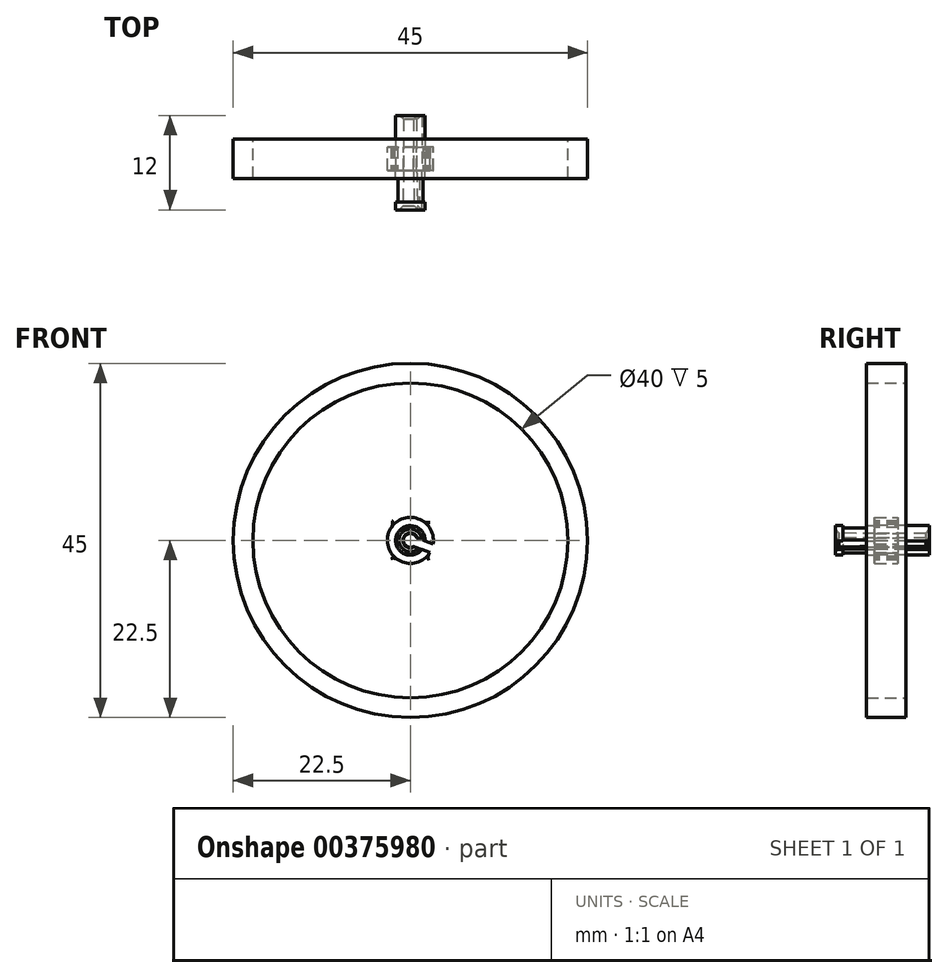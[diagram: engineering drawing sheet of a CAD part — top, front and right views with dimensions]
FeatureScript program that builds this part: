
annotation { "Feature Type Name" : "Feature", "Feature Type Description" : "" }
export const myFeature = defineFeature(function(context is Context, id is Id, definition is map)
    precondition{}
    {
        {
            var Q0;
            Q0=qCreatedBy(makeId("Front.planeOp"),FACE);
            var sketch = newSketch(context, id + "F0", { "sketchPlane" : qUnion([Q0])});
            skCircle(sketch, "E0", {"center": v(0, 0) * mm, "radius": 22.5 * mm});
            skCircle(sketch, "E1", {"center": v(0, 0) * mm, "radius": 0.88 * mm});
            skCircle(sketch, "E2", {"center": v(0, 0) * mm, "radius": 2.92 * mm});
            skCircle(sketch, "E3", {"center": v(0, 0) * mm, "radius": 20 * mm});
            skSolve(sketch);
        }
        {
            var Q0;
            Q0=qSketchRegion(id+"F0",true);
            var Q1;
            Q1=makeQuery(id+"F0.imprint","IMPRINT",FACE,{"disambiguationData":[TD([[makeQuery(id+"F0.imprint","IMPRINT",EDGE,{"derivedFrom":sQuery(id+"F0.wireOp",EDGE,"E1")}),-1.0]])]});
            extrude(context, id + "F1", {"entities" : qUnion([Q0, Q1]), "depth" : 3 * mm});
        }
        {
            var Q0;
            Q0=makeQuery(id+"F1.opExtrude","CAP_FACE",FACE,{"disambiguationData":[OSD([sQuery(id+"F0.wireOp",EDGE,"E0"),sQuery(id+"F0.wireOp",EDGE,"E3")])],"isStart":false});
            var sketch = newSketch(context, id + "F2", { "sketchPlane" : qUnion([Q0])});
            skLineSegment(sketch, "E4", {"start": v(1, 19.97) * mm, "end": v(1.93, 2.2) * mm});
            skLineSegment(sketch, "E5", {"start": v(-1, 19.97) * mm, "end": v(-1.93, 2.2) * mm});
            skLineSegment(sketch, "E6.1.0", {"start": v(-16.8, -10.85) * mm, "end": v(-0.94, -2.77) * mm});
            skLineSegment(sketch, "E6.1.1", {"start": v(-17.8, -9.12) * mm, "end": v(-2.87, 0.57) * mm});
            skLineSegment(sketch, "E6.2.0", {"start": v(17.8, -9.12) * mm, "end": v(2.87, 0.57) * mm});
            skLineSegment(sketch, "E6.2.1", {"start": v(16.8, -10.85) * mm, "end": v(0.94, -2.77) * mm});
            skPoint(sketch, "E6.center", {"position": v(0, 0) * mm});
            skArc(sketch, "E7", {"start": v(-17.8, -9.12) * mm, "mid": v(-17.32, -10) * mm, "end": v(-16.8, -10.85) * mm});
            skCircle(sketch, "E8", {"center": v(0, 0) * mm, "radius": 2.92 * mm});
            skArc(sketch, "E9.trimOffspring", {"start": v(1, 19.97) * mm, "mid": v(0, 20) * mm, "end": v(-1, 19.97) * mm});
            skArc(sketch, "E10.trimOffspring", {"start": v(16.8, -10.85) * mm, "mid": v(17.32, -10) * mm, "end": v(17.8, -9.12) * mm});
            skCircle(sketch, "E11", {"center": v(0, 0) * mm, "radius": 0.88 * mm});
            skSolve(sketch);
        }
        {
            var Q0;
            {var subQ2=sQuery(id+"F2.wireOp",EDGE,"E7");Q0=makeQuery(id+"F2.imprint","IMPRINT",FACE,{"disambiguationData":[TD([[makeQuery(id+"F2.imprint","IMPRINT",EDGE,{"derivedFrom":subQ2}),-1.0]])]});}
            var sketch = newSketch(context, id + "F3", { "sketchPlane" : qUnion([Q0])});
            skFitSpline(sketch, "E12", {"points": [v(-2.13, 2) * mm, v(-2.65, 4.3) * mm, v(-2.74, 9.9) * mm, v(0, 21.11) * mm, v(10.38, 33.43) * mm], "startDerivative": vector(-6.91, 17.48) * mm, "endDerivative": vector(42.25, 24.9) * mm});
            skFitSpline(sketch, "E13.0", {"points": [v(-0.27, 2.74) * mm, v(-0.33, 2.88) * mm, v(-0.41, 3.13) * mm, v(-0.5, 3.47) * mm, v(-0.57, 3.84) * mm, v(-0.64, 4.3) * mm, v(-0.7, 4.89) * mm, v(-0.75, 5.54) * mm, v(-0.79, 6.26) * mm, v(-0.82, 7.3) * mm, v(-0.81, 8.76) * mm, v(-0.69, 10.68) * mm, v(-0.4, 12.76) * mm, v(0.18, 15.7) * mm, v(1.13, 18.79) * mm, v(2.53, 21.89) * mm, v(4.24, 24.93) * mm, v(6.96, 28.48) * mm, v(9.8, 30.76) * mm, v(11.4, 31.7) * mm]});
            skPoint(sketch, "E14.visualSharp", {"position": v(10.36, 33.42) * mm});
            skArc(sketch, "E14.filletArc", {"start": v(7.87, 31.7) * mm, "mid": v(8.44, 32.94) * mm, "end": v(7.78, 34.12) * mm});
            skPoint(sketch, "E15.visualSharp", {"position": v(11.37, 31.7) * mm});
            skArc(sketch, "E15.filletArc", {"start": v(15.2, 31.53) * mm, "mid": v(13.12, 32.1) * mm, "end": v(11.05, 31.5) * mm});
            skArc(sketch, "E16.filletArc", {"start": v(-2.43, 1.63) * mm, "mid": v(-2.27, 2.05) * mm, "end": v(-2.3, 2.5) * mm});
            skPoint(sketch, "E17.visualSharp", {"position": v(-0.33, 2.9) * mm});
            skArc(sketch, "E17.filletArc", {"start": v(-0.46, 3.3) * mm, "mid": v(-0.28, 3.03) * mm, "end": v(0.02, 2.92) * mm});
            skArc(sketch, "E18", {"start": v(0.02, 2.92) * mm, "mid": v(-1.37, 2.59) * mm, "end": v(-2.43, 1.63) * mm});
            skArc(sketch, "E19", {"start": v(15.2, 31.53) * mm, "mid": v(11.57, 33.03) * mm, "end": v(7.78, 34.12) * mm});
            skSolve(sketch);
        }
        {
            var Q0;
            Q0=qSketchRegion(id+"F3",true);
            extrude(context, id + "F4", {"entities" : qUnion([Q0]), "oppositeDirection" : true, "depth" : 3 * mm});
        }
        {
            var Q0;
            Q0=makeQuery(id+"F4.opExtrude","SWEPT_BODY",BODY,{"disambiguationData":[OSD([sQuery(id+"F3.wireOp",EDGE,"E12"),sQuery(id+"F3.wireOp",EDGE,"E13.0"),sQuery(id+"F3.wireOp",EDGE,"E14.filletArc"),sQuery(id+"F3.wireOp",EDGE,"E15.filletArc"),sQuery(id+"F3.wireOp",EDGE,"E16.filletArc"),sQuery(id+"F3.wireOp",EDGE,"E17.filletArc"),sQuery(id+"F3.wireOp",EDGE,"E18"),sQuery(id+"F3.wireOp",EDGE,"E19")])]});
            var Q1;
            Q1=makeQuery(id+"F1.opExtrude","CAP_EDGE",EDGE,{"disambiguationData":[OSD([sQuery(id+"F0.wireOp",EDGE,"E2")])],"isStart":false});
            circularPattern(context, id + "F5", {"entities" : qUnion([Q0]), "axis" : qUnion([Q1]), "angle" : 360 * degree, "instanceCount" : 4, "equalSpace" : true});
        }
        {
            var Q0;
            Q0=makeQuery(id+"F1.opExtrude","CAP_FACE",FACE,{"disambiguationData":[OSD([sQuery(id+"F0.wireOp",EDGE,"E1"),sQuery(id+"F0.wireOp",EDGE,"E2")])],"isStart":false});
            var sketch = newSketch(context, id + "F6", { "sketchPlane" : qUnion([Q0])});
            skSolve(sketch);
        }
        {
            var Q0;
            Q0=makeQuery(id+"F6.imprint","IMPRINT",FACE,{"disambiguationData":[TD([[makeQuery(id+"F6.imprint","IMPRINT",EDGE,{"derivedFrom":makeQuery(id+"F1.opExtrude","CAP_EDGE",EDGE,{"disambiguationData":[OSD([sQuery(id+"F0.wireOp",EDGE,"E1")])],"isStart":false})}),-1.0]])]});
            var sketch = newSketch(context, id + "F7", { "sketchPlane" : qUnion([Q0])});
            skCircle(sketch, "E20.0.0", {"center": v(0, 0) * mm, "radius": 1.88 * mm});
            skSolve(sketch);
        }
        {
            var Q0;
            Q0 = qSketchRegion(id + "F7", true);
            extrude(context, id + "F8", {"entities" : qUnion([Q0]), "depth" : 5 * mm});
        }
        {
            var Q0;
            Q0=makeQuery(id+"F5.opPattern","COPY",FACE,{"derivedFrom":makeQuery(id+"F4.opExtrude","CAP_FACE",FACE,{"disambiguationData":[OSD([sQuery(id+"F3.wireOp",EDGE,"E12"),sQuery(id+"F3.wireOp",EDGE,"E13.0"),sQuery(id+"F3.wireOp",EDGE,"E14.filletArc"),sQuery(id+"F3.wireOp",EDGE,"E15.filletArc"),sQuery(id+"F3.wireOp",EDGE,"E16.filletArc"),sQuery(id+"F3.wireOp",EDGE,"E17.filletArc"),sQuery(id+"F3.wireOp",EDGE,"E18"),sQuery(id+"F3.wireOp",EDGE,"E19")])],"isStart":true}),"instanceName":"2"});
            var sketch = newSketch(context, id + "F9", { "sketchPlane" : qUnion([Q0])});
            skCircle(sketch, "E21", {"center": v(0, 0) * mm, "radius": 0.88 * mm});
            skSolve(sketch);
        }
        {
            var Q0;
            Q0 = qSketchRegion(id + "F9", true);
            extrude(context, id + "F10", {"entities" : qUnion([Q0]), "operationType" : NewBodyOperationType.REMOVE, "depth" : 25 * mm, "hasDraft" : true, "draftAngle" : 1 * degree});
        }
        {
            var Q0;
            Q0=makeQuery(id+"F6.imprint","IMPRINT",FACE,{"disambiguationData":[TD([[makeQuery(id+"F6.imprint","IMPRINT",EDGE,{"derivedFrom":makeQuery(id+"F1.opExtrude","CAP_EDGE",EDGE,{"disambiguationData":[OSD([sQuery(id+"F0.wireOp",EDGE,"E1")])],"isStart":false})}),-1.0]])]});
            var sketch = newSketch(context, id + "F11", { "sketchPlane" : qUnion([Q0])});
            skCircle(sketch, "E22.0", {"center": v(0, 0) * mm, "radius": 1.88 * mm});
            skCircle(sketch, "E23.0", {"center": v(0, 0) * mm, "radius": 0.88 * mm});
            skSolve(sketch);
        }
        {
            var Q0;
            Q0 = qSketchRegion(id + "F11", true);
            extrude(context, id + "F12", {"entities" : qUnion([Q0]), "oppositeDirection" : true, "depth" : 7 * mm});
        }
        {
            var Q0;
            Q0=makeQuery(id+"F8.opExtrude","CAP_FACE",FACE,{"disambiguationData":[OSD([sQuery(id+"F7.wireOp",EDGE,"E20.0.0")])],"isStart":false});
            var sketch = newSketch(context, id + "F13", { "sketchPlane" : qUnion([Q0])});
            skLineSegment(sketch, "E24", {"start": v(0, 0) * mm, "end": v(11.8, -4.31) * mm, "construction": true});
            skLineSegment(sketch, "E25", {"start": v(0, 0.64) * mm, "end": v(4.7, -1.08) * mm});
            skLineSegment(sketch, "E26.MirrorCS", {"start": v(-0.41, -0.49) * mm, "end": v(4.28, -2.2) * mm});
            skLineSegment(sketch, "E27", {"start": v(0, 0.64) * mm, "end": v(-0.41, -0.49) * mm});
            skLineSegment(sketch, "E28", {"start": v(4.7, -1.08) * mm, "end": v(4.28, -2.2) * mm});
            skSolve(sketch);
        }
        {
            var Q0;
            Q0 = qSketchRegion(id + "F13", true);
            extrude(context, id + "F14", {"entities" : qUnion([Q0]), "operationType" : NewBodyOperationType.REMOVE, "endBound" : BoundingType.THROUGH_ALL, "oppositeDirection" : true, "depth" : 25 * mm});
        }
        {
            var Q0;
            Q0=makeQuery(id+"F1.opExtrude","CAP_FACE",FACE,{"disambiguationData":[OSD([sQuery(id+"F0.wireOp",EDGE,"E0"),sQuery(id+"F0.wireOp",EDGE,"E3")])],"isStart":false});
            var sketch = newSketch(context, id + "F15", { "sketchPlane" : qUnion([Q0])});
            skCircle(sketch, "E29", {"center": v(0, 0) * mm, "radius": 38.67 * mm});
            skCircle(sketch, "E30", {"center": v(0, 0) * mm, "radius": 22.5 * mm});
            skSolve(sketch);
        }
        {
            var Q0;
            Q0=makeQuery(id+"F15.imprint","IMPRINT",FACE,{"disambiguationData":[TD([[makeQuery(id+"F15.imprint","IMPRINT",EDGE,{"derivedFrom":sQuery(id+"F15.wireOp",EDGE,"E29")}),1.0]])]});
            var Q1;
            Q1 = qConstructionFilter(qBodyType(qCreatedBy(id + "F15" ,EDGE), BodyType.WIRE), ConstructionObject.NO);
            extrude(context, id + "F16", {"entities" : qUnion([Q0]), "operationType" : NewBodyOperationType.REMOVE, "surfaceEntities" : qUnion([Q1]), "endBound" : BoundingType.THROUGH_ALL, "oppositeDirection" : true, "depth" : 25 * mm});
        }
        {
            var Q0;
            Q0=makeQuery(id+"F8.opExtrude","CAP_EDGE",EDGE,{"disambiguationData":[OSD([sQuery(id+"F7.wireOp",EDGE,"62ba841c-c16d-4c4f-8f28-7cdd0740cf27.0")])],"isStart":false});
            var Q1;
            Q1=makeQuery(id+"F10.boolean.opBoolean","INTERSECT",EDGE,{"derivedFrom":[makeQuery(id+"F8.opExtrude","CAP_FACE",FACE,{"disambiguationData":[OSD([sQuery(id+"F7.wireOp",EDGE,"E20.0.0")])],"isStart":false}),makeQuery(id+"F10.opExtrude","SWEPT_FACE",FACE,{"disambiguationData":[OSD([sQuery(id+"F9.wireOp",EDGE,"E21")])]})]});
            var Q2;
            Q2=makeQuery(id+"F12.opExtrude","CAP_EDGE",EDGE,{"disambiguationData":[OSD([sQuery(id+"F11.wireOp",EDGE,"E23.0")])],"isStart":false});
            chamfer(context, id + "F17", {"entities" : qUnion([Q0, Q1, Q2]), "width" : .5 * mm, "tangentPropagation" : true});
        }
        {
            var Q0;
            Q0=makeQuery(id+"F1.opExtrude","CAP_FACE",FACE,{"disambiguationData":[OSD([sQuery(id+"F0.wireOp",EDGE,"E0"),sQuery(id+"F0.wireOp",EDGE,"E3")])],"isStart":true});
            var sketch = newSketch(context, id + "F18", { "sketchPlane" : qUnion([Q0])});
            skCircle(sketch, "E31.0.0", {"center": v(0, 0) * mm, "radius": 22.5 * mm});
            skCircle(sketch, "E32.0", {"center": v(0, 0) * mm, "radius": 20 * mm});
            skSolve(sketch);
        }
        {
            var Q0;
            Q0 = qSketchRegion(id + "F18", true);
            extrude(context, id + "F19", {"entities" : qUnion([Q0]), "operationType" : NewBodyOperationType.ADD, "depth" : 1 * mm, "hasSecondDirection" : true, "secondDirectionOppositeDirection" : true, "secondDirectionDepth" : 4 * mm});
        }
        {
            var Q0;
            Q0=makeQuery(id+"F8.opExtrude","CAP_FACE",FACE,{"disambiguationData":[OSD([sQuery(id+"F7.wireOp",EDGE,"E20.0.0")])],"isStart":false});
            var sketch = newSketch(context, id + "F20", { "sketchPlane" : qUnion([Q0])});
            skCircle(sketch, "E33", {"center": v(0, 0) * mm, "radius": 1.57 * mm});
            skCircle(sketch, "E34", {"center": v(0, 0) * mm, "radius": 1.88 * mm});
            skSolve(sketch);
        }
        {
            var Q0;
            Q0 = qSketchRegion(id + "F20", true);
            extrude(context, id + "F21", {"entities" : qUnion([Q0]), "operationType" : NewBodyOperationType.REMOVE, "oppositeDirection" : true, "depth" : 4 * mm, "hasSecondDirection" : true, "secondDirectionOppositeDirection" : true, "secondDirectionDepth" : 1 * mm});
        }
    });
